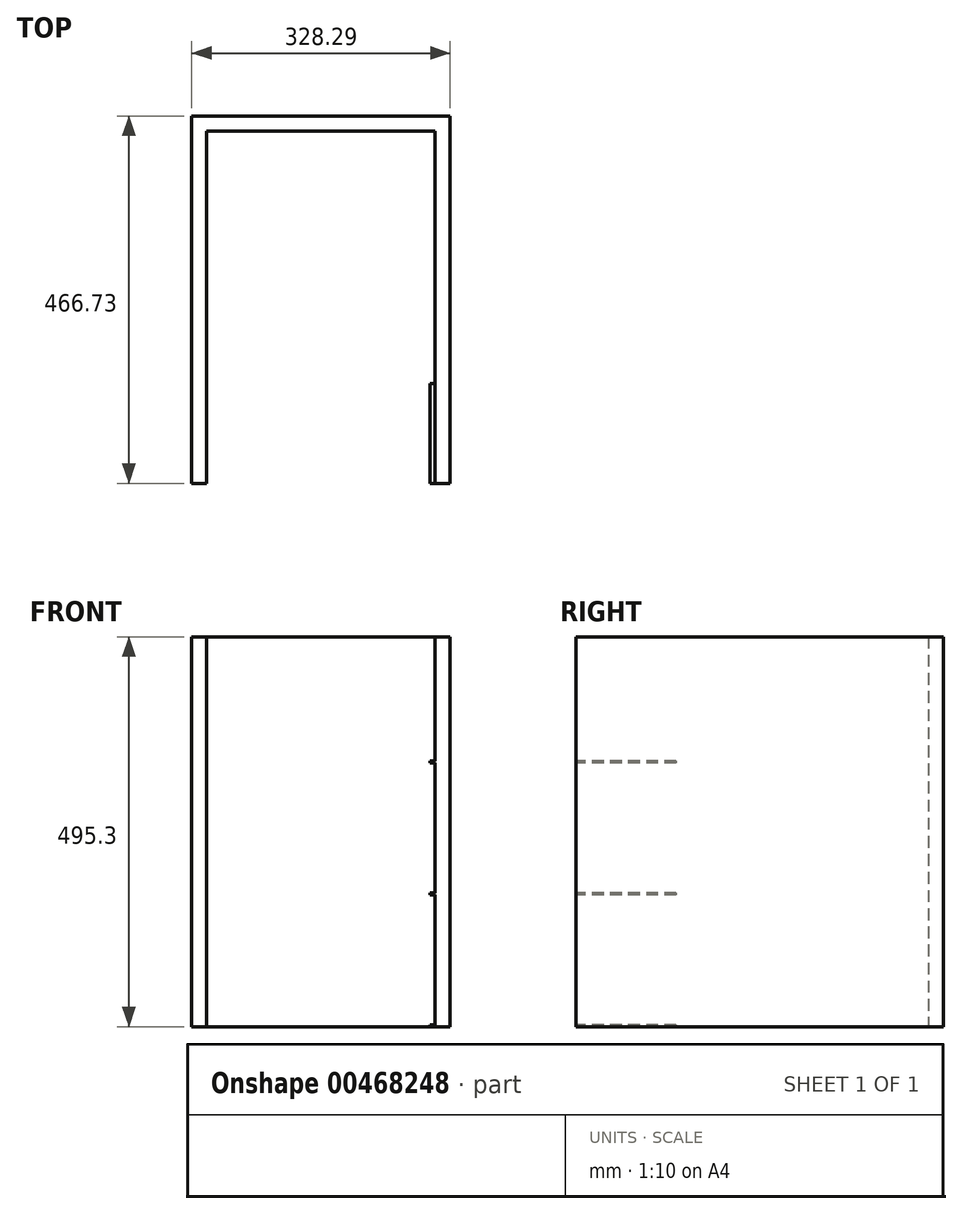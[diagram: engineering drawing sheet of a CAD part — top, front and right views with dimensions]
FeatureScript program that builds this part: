
annotation { "Feature Type Name" : "Feature", "Feature Type Description" : "" }
export const myFeature = defineFeature(function(context is Context, id is Id, definition is map)
    precondition{}
    {
        {
            var Q0;
            Q0=qCreatedBy(makeId("Top.planeOp"),FACE);
            var sketch = newSketch(context, id + "F0", { "sketchPlane" : qUnion([Q0])});
            skLineSegment(sketch, "E0.bottom", {"start": v(0, 0) * mm, "end": v(-244.47, 0) * mm});
            skLineSegment(sketch, "E0.top", {"start": v(0, -422.28) * mm, "end": v(-244.47, -422.28) * mm});
            skLineSegment(sketch, "E0.left", {"start": v(0, 0) * mm, "end": v(0, -422.28) * mm});
            skLineSegment(sketch, "E0.right", {"start": v(-244.47, 0) * mm, "end": v(-244.47, -422.28) * mm});
            skLineSegment(sketch, "E1.0", {"start": v(12.7, -434.98) * mm, "end": v(-257.17, -434.98) * mm});
            skLineSegment(sketch, "E1.1", {"start": v(12.7, 12.7) * mm, "end": v(12.7, -434.98) * mm});
            skLineSegment(sketch, "E1.2", {"start": v(12.7, 12.7) * mm, "end": v(-257.18, 12.7) * mm});
            skLineSegment(sketch, "E1.3", {"start": v(-257.18, 12.7) * mm, "end": v(-257.17, -434.98) * mm});
            skLineSegment(sketch, "E2", {"start": v(-267.33, -434.98) * mm, "end": v(-267.33, 12.7) * mm});
            skLineSegment(sketch, "E3", {"start": v(-267.33, 12.7) * mm, "end": v(22.86, 12.7) * mm});
            skLineSegment(sketch, "E4", {"start": v(22.86, 12.7) * mm, "end": v(22.86, -434.98) * mm});
            skLineSegment(sketch, "E5", {"start": v(22.86, -434.98) * mm, "end": v(41.91, -434.97) * mm});
            skLineSegment(sketch, "E6", {"start": v(41.91, -434.97) * mm, "end": v(41.91, 31.75) * mm});
            skLineSegment(sketch, "E7", {"start": v(41.91, 31.75) * mm, "end": v(-286.38, 31.75) * mm});
            skLineSegment(sketch, "E8", {"start": v(-286.38, 31.75) * mm, "end": v(-286.38, -434.98) * mm});
            skLineSegment(sketch, "E9", {"start": v(-286.38, -434.98) * mm, "end": v(-267.33, -434.98) * mm});
            skSolve(sketch);
        }
        {
            var Q0;
            {var subQ4=sQuery(id+"F0.wireOp",EDGE,"E2");Q0=makeQuery(id+"F0.imprint","IMPRINT",FACE,{"disambiguationData":[TD([[makeQuery(id+"F0.imprint","IMPRINT",EDGE,{"derivedFrom":subQ4}),1.0]])]});}
            extrude(context, id + "F1", {"entities" : qUnion([Q0]), "depth" : 495.3 * mm});
        }
        {
            var Q0;
            Q0=makeQuery(id+"F1.opExtrude","SWEPT_FACE",FACE,{"disambiguationData":[OSD([sQuery(id+"F0.wireOp",EDGE,"E5")])]});
            var sketch = newSketch(context, id + "F2", { "sketchPlane" : qUnion([Q0])});
            skLineSegment(sketch, "E10.bottom", {"start": v(22.86, 0) * mm, "end": v(16.5, 0) * mm});
            skLineSegment(sketch, "E10.top", {"start": v(22.86, 2.54) * mm, "end": v(16.5, 2.54) * mm});
            skLineSegment(sketch, "E10.left", {"start": v(22.86, 0) * mm, "end": v(22.86, 2.54) * mm});
            skLineSegment(sketch, "E10.right", {"start": v(16.5, 0) * mm, "end": v(16.5, 2.54) * mm});
            skLineSegment(sketch, "E11.bottom", {"start": v(22.86, 170.18) * mm, "end": v(16.5, 170.18) * mm});
            skLineSegment(sketch, "E11.top", {"start": v(22.86, 167.64) * mm, "end": v(16.5, 167.64) * mm});
            skLineSegment(sketch, "E11.left", {"start": v(22.86, 170.18) * mm, "end": v(22.86, 167.64) * mm});
            skLineSegment(sketch, "E11.right", {"start": v(16.5, 170.18) * mm, "end": v(16.5, 167.64) * mm});
            skLineSegment(sketch, "E12.bottom", {"start": v(22.86, 337.82) * mm, "end": v(16.5, 337.82) * mm});
            skLineSegment(sketch, "E12.top", {"start": v(22.86, 335.28) * mm, "end": v(16.5, 335.28) * mm});
            skLineSegment(sketch, "E12.left", {"start": v(22.86, 337.82) * mm, "end": v(22.86, 335.28) * mm});
            skLineSegment(sketch, "E12.right", {"start": v(16.5, 337.82) * mm, "end": v(16.5, 335.28) * mm});
            skSolve(sketch);
        }
        {
            var Q0;
            Q0=qSketchRegion(id+"F2",true);
            extrude(context, id + "F3", {"entities" : qUnion([Q0]), "operationType" : NewBodyOperationType.ADD, "oppositeDirection" : true, "depth" : 127 * mm});
        }
    });
